# Revit family: PRD_AR_TwlRls_SaturnTowelRailForWashingTroughs_TB60,70,80
name_source: partatom
category: Furniture
revit_build: Autodesk Revit 2018 (Build: 20190510_1515(x64)
units: mm (PartAtom-declared; Revit-internal decimal feet)

## family parameters
Always vertical = No
Cut with Voids When Loaded = No
OmniClass Number = 23.40.20.21
OmniClass Title = Toilet and Bath Specialties
Room Calculation Point = No
Shared = Yes
Work Plane-Based = Yes

## types (2) — shared parameters
AssetType = Fixed
Category = Pr_40_20_76_90, Towel rails
Color = Stainless steel
Default Elevation = 1219 mm
DurationUnit = year
Finish = Satin finished
FinishAndColour = Stainless steel, satin finished
Form = Mounted on product
IfcExportAs = IfcFurnitureType
IfcExportType = NOTDEFINED
MainColor = Stainless steel
Manufacturer = KWC Group AG
ManufacturerName = KWC Group AG
ManufacturerURL = www.kwc.com
Material = Stainless steel
Materials = Stainless steel 1.4301
NBSDescription = Towel rails
NBSReference = 45-35-72/372
NominalDepth = 8 mm  [stored 0.0262467 ft]
NominalHeight = 119 mm  [stored 0.39042 ft]
ProductInformation = https://pim.kwc.com
Shape = Rectangular
Style = Towel rail
TowelRailMaterial = PRD_AR_StainlessSteel_SatinFinished
URL = www.kwc.com
Uniclass2015Code = Pr_40_20_76_90
Uniclass2015Title = Towel rails
Uniclass2015Version = Products v1.10
Version = 1
WarrantyDurationUnit = year
zero-valued in all types: NominalWidth

## per-type parameters (varying)
| type | BIMObjectName | Description | Features | GrossWeight | IntegralAccessories | Model | ModelNumber | ModelReference | Name | NetWeight | NominalLength | Size |
| TB60 - L=478 | PRD_AR_TowelRails_SaturnTowelRailForWashingTroughs_TB60 | Towel rail for KWC washing troughs ECO400CS, BX400CNS and ECN400CNS, stainless steel, surface satin finished, material thickness 8 mm, for mounting underneath front edge, rail is flexible and retrofittable, one set per wash place necessary, incl. mounting set. width: 478 mm | stainless steel, 8 mm, satin finished, mounted on product, 478x119x8 mm (WxHxD) | 0.70 kg | incl. mounting set | TB60 | 2000101452 | TB60 | SATURN towel rail for washing troughs TB60 | 0.50 kg | 478 mm  [stored 1.56824 ft] | 119 x 478 x 8 mm |
| TB80 - L=728 | PRD_AR_TowelRails_SaturnTowelRailForWashingTroughs_TB80 | Towel rail for KWCe washtroughs BX, ECN, ECO and PLANOX, stainless steel, surface satin finished, material thickness ⌀8 mm, for mounting underneath front edge, rail is flexible and retrofittable, one set per wash place necessary, inclusive mounting set. | stainless steel, 8 mm, satin finished, mounted on product, 728x119x8 mm (WxHxD) | 0.80 kg | Incl. mounting set | TB80 | 2030046200 | TB80 | SATURN towel rail for washing troughs TB80 | 0.30 kg | 728 mm  [stored 2.38845 ft] | 119 x 728 x 8 mm |

note: [stored X ft] marks values corroborated as IEEE doubles in the binary element streams (Revit-internal decimal feet)

## geometry (parser evidence)
native form markers: Sweep x2
no freeform markers — native parametric forms only
